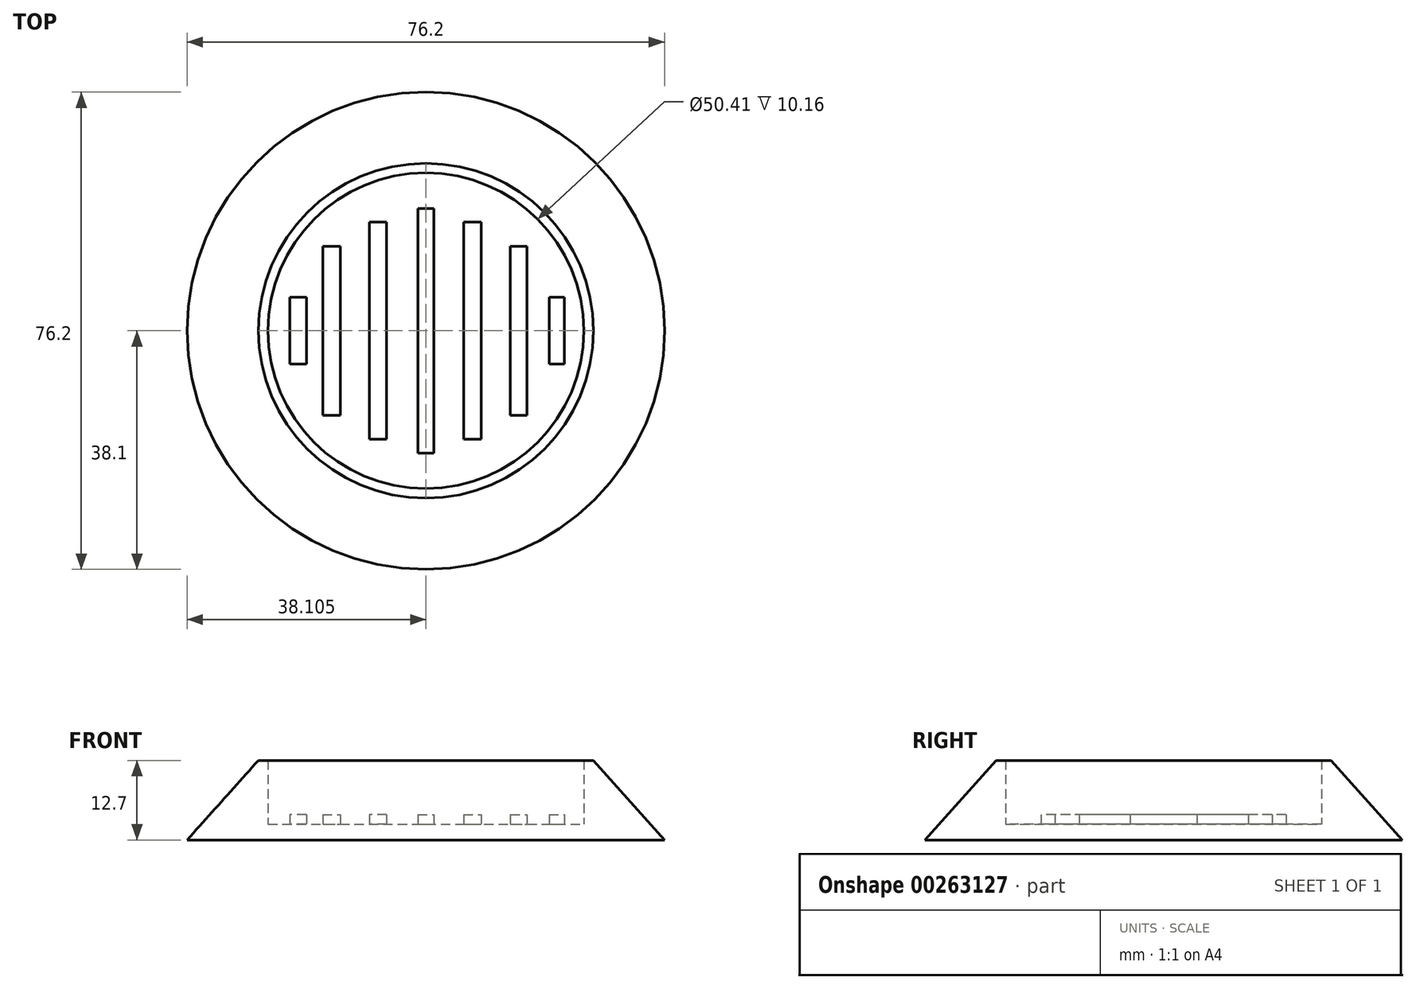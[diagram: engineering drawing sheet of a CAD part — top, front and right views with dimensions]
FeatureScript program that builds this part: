
annotation { "Feature Type Name" : "Feature", "Feature Type Description" : "" }
export const myFeature = defineFeature(function(context is Context, id is Id, definition is map)
    precondition{}
    {
        {
            var Q0;
            Q0=qCreatedBy(makeId("Front.planeOp"),FACE);
            var sketch = newSketch(context, id + "F0", { "sketchPlane" : qUnion([Q0])});
            skLineSegment(sketch, "E0", {"start": v(-1.52, 30.27) * mm, "end": v(-12.9, 17.57) * mm});
            skLineSegment(sketch, "E1", {"start": v(-12.9, 17.57) * mm, "end": v(25.2, 17.57) * mm});
            skLineSegment(sketch, "E2", {"start": v(25.2, 17.57) * mm, "end": v(25.2, 20.11) * mm});
            skLineSegment(sketch, "E3", {"start": v(25.2, 20.11) * mm, "end": v(0, 20.11) * mm});
            skLineSegment(sketch, "E4", {"start": v(0, 20.11) * mm, "end": v(0, 30.27) * mm});
            skLineSegment(sketch, "E5", {"start": v(0, 30.27) * mm, "end": v(-1.52, 30.27) * mm});
            skSolve(sketch);
        }
        {
            var Q0;
            Q0=makeQuery(id+"F0.imprint","IMPRINT",FACE,{"disambiguationData":[TD([[makeQuery(id+"F0.imprint","IMPRINT",EDGE,{"derivedFrom":sQuery(id+"F0.wireOp",EDGE,"E0")}),1.0]])]});
            var Q1;
            Q1=sQuery(id+"F0.wireOp",EDGE,"E2");
            revolve(context, id + "F1", {"entities" : qUnion([Q0]), "axis" : qUnion([Q1]), "revolveType" : RevolveType.FULL});
        }
        {
            var Q0;
            Q0=makeQuery(id+"F1.opRevolve","SWEPT_FACE",FACE,{"disambiguationData":[OSD([sQuery(id+"F0.wireOp",EDGE,"E3")])]});
            var sketch = newSketch(context, id + "F2", { "sketchPlane" : qUnion([Q0])});
            skLineSegment(sketch, "E6.bottom", {"start": v(23.92, 19.54) * mm, "end": v(26.5, 19.54) * mm});
            skLineSegment(sketch, "E6.top", {"start": v(23.92, -19.54) * mm, "end": v(26.5, -19.54) * mm});
            skLineSegment(sketch, "E6.left", {"start": v(23.92, 19.54) * mm, "end": v(23.92, -19.54) * mm});
            skLineSegment(sketch, "E6.right", {"start": v(26.5, 19.54) * mm, "end": v(26.5, -19.54) * mm});
            skPoint(sketch, "E6.middle", {"position": v(25.2, 0) * mm});
            skLineSegment(sketch, "E7.bottom", {"start": v(18.94, 17.33) * mm, "end": v(16.21, 17.33) * mm});
            skLineSegment(sketch, "E7.top", {"start": v(18.94, -17.33) * mm, "end": v(16.21, -17.33) * mm});
            skLineSegment(sketch, "E7.left", {"start": v(16.21, 17.33) * mm, "end": v(16.21, -17.33) * mm});
            skLineSegment(sketch, "E7.right", {"start": v(18.94, 17.33) * mm, "end": v(18.94, -17.33) * mm});
            skPoint(sketch, "E7.middle", {"position": v(17.58, 0) * mm});
            skPoint(sketch, "E7.middle.positionSnap0", {"position": v(23.92, 0) * mm});
            skPoint(sketch, "E7.centerSnap0", {"position": v(23.92, 0) * mm});
            skLineSegment(sketch, "E8.bottom", {"start": v(31.23, 17.33) * mm, "end": v(34.06, 17.33) * mm});
            skLineSegment(sketch, "E8.top", {"start": v(31.23, -17.33) * mm, "end": v(34.06, -17.33) * mm});
            skLineSegment(sketch, "E8.left", {"start": v(31.23, 17.33) * mm, "end": v(31.23, -17.33) * mm});
            skLineSegment(sketch, "E8.right", {"start": v(34.06, 17.33) * mm, "end": v(34.06, -17.33) * mm});
            skPoint(sketch, "E8.middle", {"position": v(32.64, 0) * mm});
            skLineSegment(sketch, "E9.bottom", {"start": v(8.76, 13.5) * mm, "end": v(11.58, 13.5) * mm});
            skLineSegment(sketch, "E9.top", {"start": v(8.76, -13.5) * mm, "end": v(11.58, -13.5) * mm});
            skLineSegment(sketch, "E9.left", {"start": v(8.76, 13.5) * mm, "end": v(8.76, -13.5) * mm});
            skLineSegment(sketch, "E9.right", {"start": v(11.58, 13.5) * mm, "end": v(11.58, -13.5) * mm});
            skPoint(sketch, "E9.middle", {"position": v(10.17, 0) * mm});
            skPoint(sketch, "E9.middle.positionSnap0", {"position": v(18.94, 0) * mm});
            skPoint(sketch, "E9.centerSnap0", {"position": v(18.94, 0) * mm});
            skLineSegment(sketch, "E10.bottom", {"start": v(38.7, 13.5) * mm, "end": v(41.31, 13.5) * mm});
            skLineSegment(sketch, "E10.top", {"start": v(38.7, -13.5) * mm, "end": v(41.31, -13.5) * mm});
            skLineSegment(sketch, "E10.left", {"start": v(38.7, 13.5) * mm, "end": v(38.7, -13.5) * mm});
            skLineSegment(sketch, "E10.right", {"start": v(41.31, 13.5) * mm, "end": v(41.31, -13.5) * mm});
            skPoint(sketch, "E10.middle", {"position": v(40, 0) * mm});
            skLineSegment(sketch, "E11.bottom", {"start": v(6.13, 5.33) * mm, "end": v(3.51, 5.33) * mm});
            skLineSegment(sketch, "E11.top", {"start": v(6.13, -5.33) * mm, "end": v(3.51, -5.33) * mm});
            skLineSegment(sketch, "E11.left", {"start": v(6.13, 5.33) * mm, "end": v(6.13, -5.33) * mm});
            skLineSegment(sketch, "E11.right", {"start": v(3.51, 5.33) * mm, "end": v(3.51, -5.33) * mm});
            skPoint(sketch, "E11.middle", {"position": v(4.82, 0) * mm});
            skLineSegment(sketch, "E12.bottom", {"start": v(44.86, 5.33) * mm, "end": v(47.28, 5.33) * mm});
            skLineSegment(sketch, "E12.top", {"start": v(44.86, -5.33) * mm, "end": v(47.28, -5.33) * mm});
            skLineSegment(sketch, "E12.left", {"start": v(44.86, 5.33) * mm, "end": v(44.86, -5.33) * mm});
            skLineSegment(sketch, "E12.right", {"start": v(47.28, 5.33) * mm, "end": v(47.28, -5.33) * mm});
            skPoint(sketch, "E12.middle", {"position": v(46.07, 0) * mm});
            skSolve(sketch);
        }
        {
            var Q0;
            Q0=makeQuery(id+"F2.imprint","IMPRINT",FACE,{"disambiguationData":[TD([[makeQuery(id+"F2.imprint","IMPRINT",EDGE,{"derivedFrom":sQuery(id+"F2.wireOp",EDGE,"E6.bottom")}),-1.0]])]});
            var Q1;
            Q1=makeQuery(id+"F2.imprint","IMPRINT",FACE,{"disambiguationData":[TD([[makeQuery(id+"F2.imprint","IMPRINT",EDGE,{"derivedFrom":sQuery(id+"F2.wireOp",EDGE,"E8.bottom")}),-1.0]])]});
            var Q2;
            Q2=makeQuery(id+"F2.imprint","IMPRINT",FACE,{"disambiguationData":[TD([[makeQuery(id+"F2.imprint","IMPRINT",EDGE,{"derivedFrom":sQuery(id+"F2.wireOp",EDGE,"E10.bottom")}),-1.0]])]});
            var Q3;
            Q3=makeQuery(id+"F2.imprint","IMPRINT",FACE,{"disambiguationData":[TD([[makeQuery(id+"F2.imprint","IMPRINT",EDGE,{"derivedFrom":sQuery(id+"F2.wireOp",EDGE,"E12.bottom")}),-1.0]])]});
            var Q4;
            Q4=makeQuery(id+"F2.imprint","IMPRINT",FACE,{"disambiguationData":[TD([[makeQuery(id+"F2.imprint","IMPRINT",EDGE,{"derivedFrom":sQuery(id+"F2.wireOp",EDGE,"E7.bottom")}),1.0]])]});
            var Q5;
            Q5=makeQuery(id+"F2.imprint","IMPRINT",FACE,{"disambiguationData":[TD([[makeQuery(id+"F2.imprint","IMPRINT",EDGE,{"derivedFrom":sQuery(id+"F2.wireOp",EDGE,"E9.bottom")}),-1.0]])]});
            var Q6;
            Q6=makeQuery(id+"F2.imprint","IMPRINT",FACE,{"disambiguationData":[TD([[makeQuery(id+"F2.imprint","IMPRINT",EDGE,{"derivedFrom":sQuery(id+"F2.wireOp",EDGE,"E11.bottom")}),1.0]])]});
            extrude(context, id + "F3", {"entities" : qUnion([Q0, Q1, Q2, Q3, Q4, Q5, Q6]), "operationType" : NewBodyOperationType.ADD, "depth" : 1.52 * mm});
        }
    });
